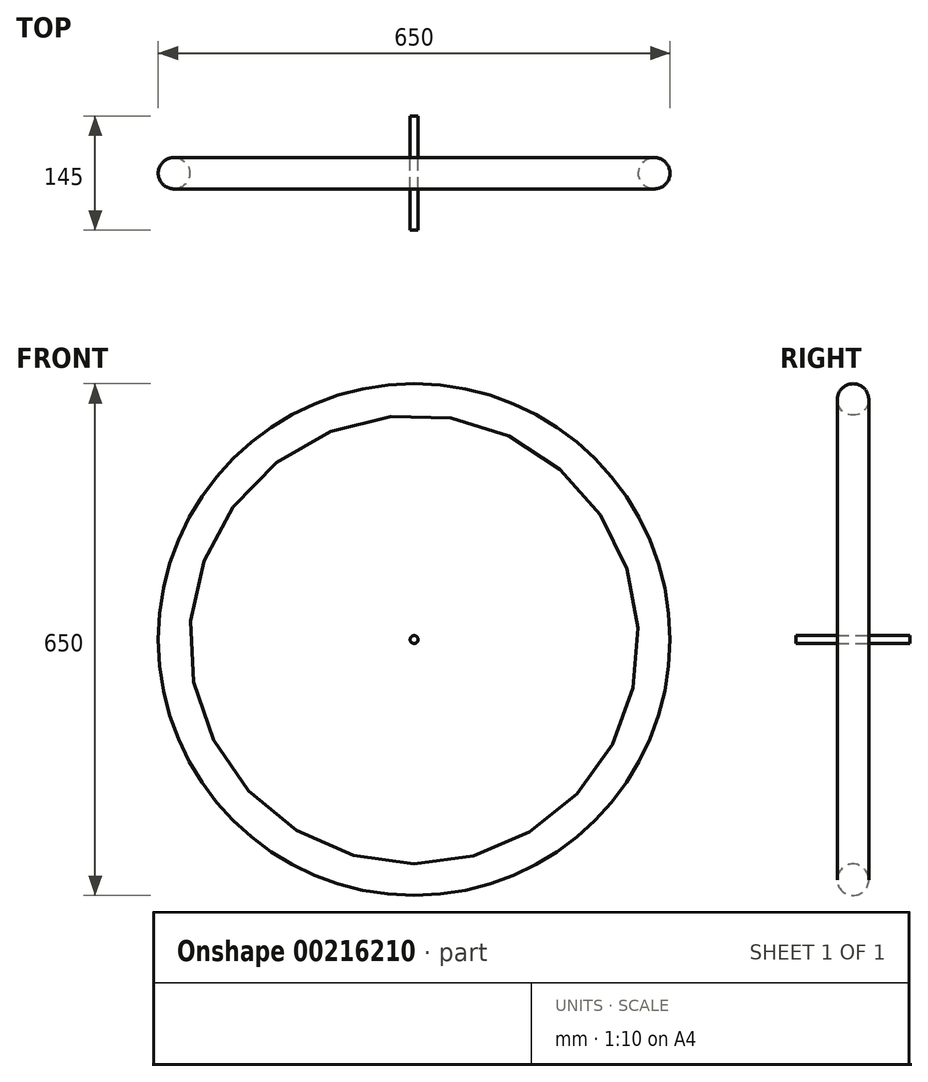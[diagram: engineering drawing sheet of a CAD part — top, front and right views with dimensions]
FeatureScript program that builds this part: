
annotation { "Feature Type Name" : "Feature", "Feature Type Description" : "" }
export const myFeature = defineFeature(function(context is Context, id is Id, definition is map)
    precondition{}
    {
        {
            var Q0;
            Q0=qCreatedBy(makeId("Top.planeOp"),FACE);
            var sketch = newSketch(context, id + "F0", { "sketchPlane" : qUnion([Q0])});
            skLineSegment(sketch, "E0", {"start": v(0, 0) * mm, "end": v(305, 0) * mm, "construction": true});
            skCircle(sketch, "E1", {"center": v(305, 0) * mm, "radius": 20 * mm});
            skLineSegment(sketch, "E2", {"start": v(0, 0) * mm, "end": v(0, 35.05) * mm, "construction": true});
            skSolve(sketch);
        }
        {
            var Q0;
            Q0=makeQuery(id+"F0.imprint","IMPRINT",FACE,{"disambiguationData":[TD([[makeQuery(id+"F0.imprint","IMPRINT",EDGE,{"derivedFrom":sQuery(id+"F0.wireOp",EDGE,"E1")}),1.0]])]});
            var Q1;
            Q1=sQuery(id+"F0.wireOp",EDGE,"E2");
            revolve(context, id + "F1", {"entities" : qUnion([Q0]), "axis" : qUnion([Q1]), "revolveType" : RevolveType.FULL});
        }
        {
            var Q0;
            Q0=qCreatedBy(makeId("Front.planeOp"),FACE);
            var sketch = newSketch(context, id + "F2", { "sketchPlane" : qUnion([Q0])});
            skCircle(sketch, "E3", {"center": v(0, 0) * mm, "radius": 5 * mm});
            skSolve(sketch);
        }
        {
            var Q0;
            Q0=makeQuery(id+"F2.imprint","IMPRINT",FACE,{"disambiguationData":[TD([[makeQuery(id+"F2.imprint","IMPRINT",EDGE,{"derivedFrom":sQuery(id+"F2.wireOp",EDGE,"E3")}),1.0]])]});
            extrude(context, id + "F3", {"entities" : qUnion([Q0]), "depth" : 145 * mm, "symmetric" : true});
        }
    });
